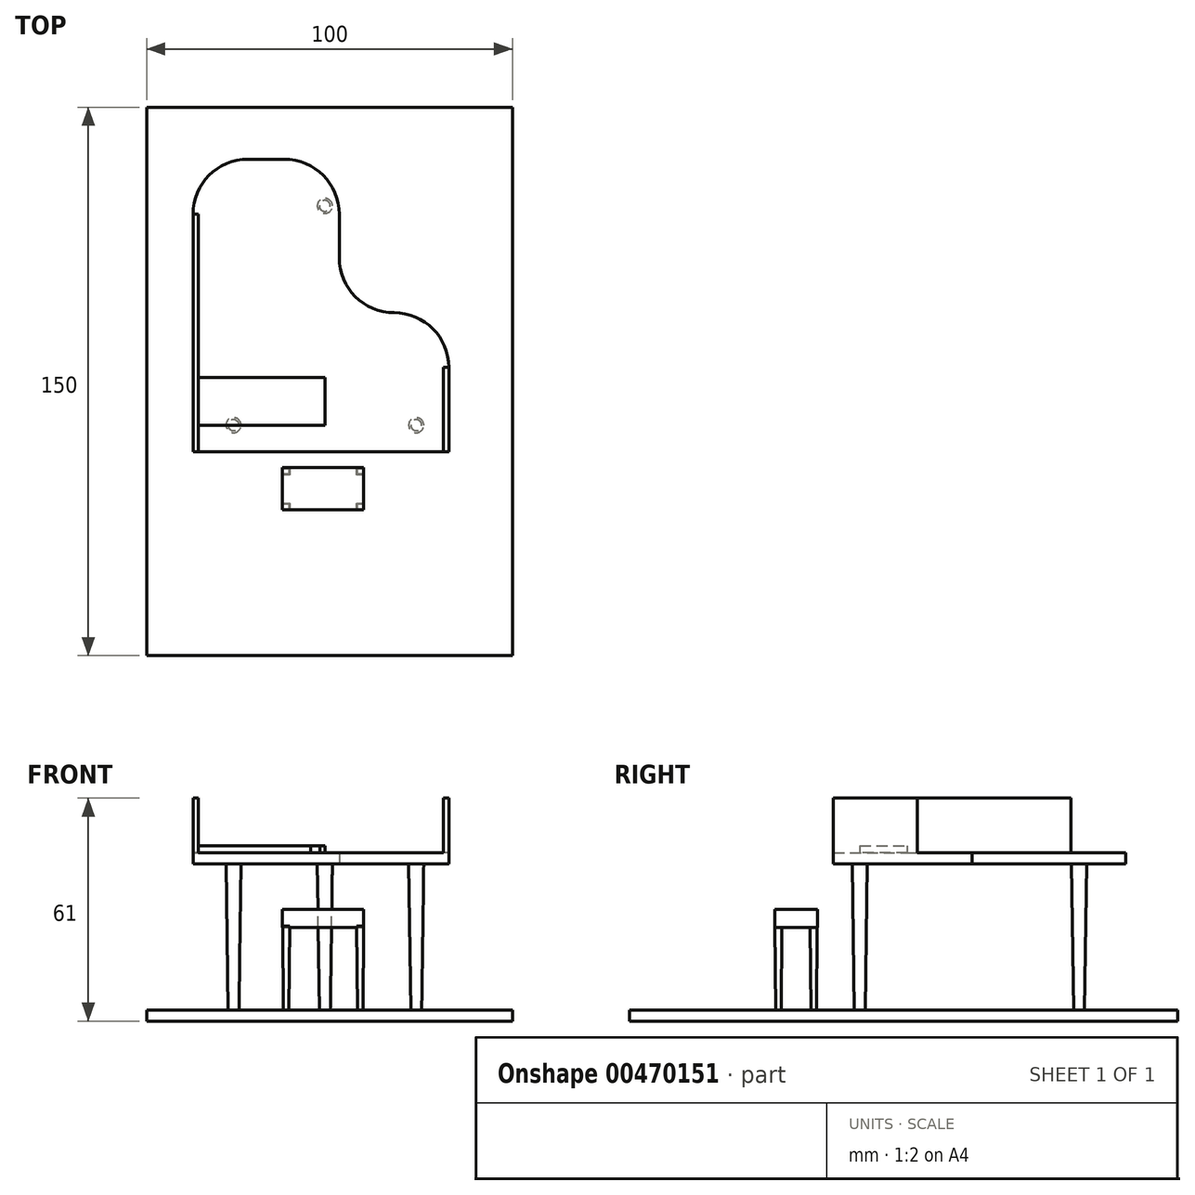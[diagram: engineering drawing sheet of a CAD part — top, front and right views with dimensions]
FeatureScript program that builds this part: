
annotation { "Feature Type Name" : "Feature", "Feature Type Description" : "" }
export const myFeature = defineFeature(function(context is Context, id is Id, definition is map)
    precondition{}
    {
        {
            var Q0;
            Q0=qCreatedBy(makeId("Top.planeOp"),FACE);
            var sketch = newSketch(context, id + "F0", { "sketchPlane" : qUnion([Q0])});
            skLineSegment(sketch, "E0.bottom", {"start": v(-48.7, 86.94) * mm, "end": v(51.3, 86.94) * mm});
            skLineSegment(sketch, "E0.top", {"start": v(-48.7, -63.06) * mm, "end": v(51.3, -63.06) * mm});
            skLineSegment(sketch, "E0.left", {"start": v(-48.7, 86.94) * mm, "end": v(-48.7, -63.06) * mm});
            skLineSegment(sketch, "E0.right", {"start": v(51.3, 86.94) * mm, "end": v(51.3, -63.06) * mm});
            skSolve(sketch);
        }
        {
            var Q0;
            Q0 = qSketchRegion(id + "F0", true);
            extrude(context, id + "F1", {"entities" : qUnion([Q0]), "depth" : 3 * mm});
        }
        {
            var Q0;
            Q0=makeQuery(id+"F1.opExtrude","CAP_FACE",FACE,{"disambiguationData":[OSD([sQuery(id+"F0.wireOp",EDGE,"E0.bottom"),sQuery(id+"F0.wireOp",EDGE,"E0.top"),sQuery(id+"F0.wireOp",EDGE,"E0.left"),sQuery(id+"F0.wireOp",EDGE,"E0.right")])],"isStart":false});
            var sketch = newSketch(context, id + "F2", { "sketchPlane" : qUnion([Q0])});
            skCircle(sketch, "E1", {"center": v(0, 60) * mm, "radius": 1.5 * mm});
            skCircle(sketch, "E2", {"center": v(-25, 0) * mm, "radius": 1.5 * mm});
            skCircle(sketch, "E3", {"center": v(25, 0) * mm, "radius": 1.5 * mm});
            skSolve(sketch);
        }
        {
            var Q0;
            Q0 = qSketchRegion(id + "F2", true);
            extrude(context, id + "F3", {"entities" : qUnion([Q0]), "operationType" : NewBodyOperationType.ADD, "depth" : 40 * mm, "hasDraft" : true, "draftAngle" : 0.8 * degree});
        }
        {
            var Q0;
            Q0=makeQuery(id+"F2.imprint","IMPRINT",FACE,{"disambiguationData":[TD([[makeQuery(id+"F2.imprint","IMPRINT",EDGE,{"derivedFrom":sQuery(id+"F2.wireOp",EDGE,"E1")}),-1.0]])]});
            var sketch = newSketch(context, id + "F4", { "sketchPlane" : qUnion([Q0])});
            skLineSegment(sketch, "E4.bottom", {"start": v(-11.36, -11.88) * mm, "end": v(-9.86, -11.88) * mm});
            skLineSegment(sketch, "E4.top", {"start": v(-11.36, -13.38) * mm, "end": v(-9.86, -13.38) * mm});
            skLineSegment(sketch, "E4.left", {"start": v(-11.36, -11.88) * mm, "end": v(-11.36, -13.38) * mm});
            skLineSegment(sketch, "E4.right", {"start": v(-9.86, -11.88) * mm, "end": v(-9.86, -13.38) * mm});
            skLineSegment(sketch, "E5.bottom", {"start": v(8.92, -11.88) * mm, "end": v(10.42, -11.88) * mm});
            skLineSegment(sketch, "E5.top", {"start": v(8.92, -13.38) * mm, "end": v(10.42, -13.38) * mm});
            skLineSegment(sketch, "E5.left", {"start": v(8.92, -11.88) * mm, "end": v(8.92, -13.38) * mm});
            skLineSegment(sketch, "E5.right", {"start": v(10.42, -11.88) * mm, "end": v(10.42, -13.38) * mm});
            skLineSegment(sketch, "E6.bottom", {"start": v(-11.36, -21.51) * mm, "end": v(-9.86, -21.51) * mm});
            skLineSegment(sketch, "E6.top", {"start": v(-11.36, -23.01) * mm, "end": v(-9.86, -23.01) * mm});
            skLineSegment(sketch, "E6.left", {"start": v(-11.36, -21.51) * mm, "end": v(-11.36, -23.01) * mm});
            skLineSegment(sketch, "E6.right", {"start": v(-9.86, -21.51) * mm, "end": v(-9.86, -23.01) * mm});
            skLineSegment(sketch, "E7.bottom", {"start": v(10.42, -21.51) * mm, "end": v(8.92, -21.51) * mm});
            skLineSegment(sketch, "E7.top", {"start": v(10.42, -23.01) * mm, "end": v(8.92, -23.01) * mm});
            skLineSegment(sketch, "E7.left", {"start": v(10.42, -21.51) * mm, "end": v(10.42, -23.01) * mm});
            skLineSegment(sketch, "E7.right", {"start": v(8.92, -21.51) * mm, "end": v(8.92, -23.01) * mm});
            skSolve(sketch);
        }
        {
            var Q0;
            Q0 = qSketchRegion(id + "F4", true);
            extrude(context, id + "F5", {"entities" : qUnion([Q0]), "operationType" : NewBodyOperationType.ADD, "depth" : 23 * mm, "hasDraft" : true, "draftAngle" : 0.5 * degree});
        }
        {
            var Q0;
            Q0=makeQuery(id+"F5.opExtrude","CAP_FACE",FACE,{"disambiguationData":[OSD([sQuery(id+"F4.wireOp",EDGE,"E4.bottom"),sQuery(id+"F4.wireOp",EDGE,"E4.top"),sQuery(id+"F4.wireOp",EDGE,"E4.left"),sQuery(id+"F4.wireOp",EDGE,"E4.right")])],"isStart":false});
            var sketch = newSketch(context, id + "F6", { "sketchPlane" : qUnion([Q0])});
            skLineSegment(sketch, "E8.bottom", {"start": v(-11.6, -11.63) * mm, "end": v(10.64, -11.63) * mm});
            skLineSegment(sketch, "E8.top", {"start": v(-11.6, -23.19) * mm, "end": v(10.64, -23.19) * mm});
            skLineSegment(sketch, "E8.left", {"start": v(-11.6, -11.63) * mm, "end": v(-11.6, -23.19) * mm});
            skLineSegment(sketch, "E8.right", {"start": v(10.64, -11.63) * mm, "end": v(10.64, -23.19) * mm});
            skSolve(sketch);
        }
        {
            var Q0;
            Q0 = qSketchRegion(id + "F6", true);
            extrude(context, id + "F7", {"entities" : qUnion([Q0]), "operationType" : NewBodyOperationType.ADD, "depth" : 4.6 * mm, "hasSecondDirection" : true, "secondDirectionOppositeDirection" : true, "secondDirectionDepth" : 0.4 * mm});
        }
        {
            var Q0;
            Q0=makeQuery(id+"F3.opExtrude","CAP_FACE",FACE,{"disambiguationData":[OSD([sQuery(id+"F2.wireOp",EDGE,"E1")])],"isStart":false});
            var sketch = newSketch(context, id + "F8", { "sketchPlane" : qUnion([Q0])});
            skLineSegment(sketch, "E9", {"start": v(-36.08, -7.22) * mm, "end": v(-36.08, 57.78) * mm});
            skLineSegment(sketch, "E10", {"start": v(-36.08, -7.22) * mm, "end": v(33.92, -7.22) * mm});
            skLineSegment(sketch, "E11", {"start": v(-21.08, 72.78) * mm, "end": v(-11.08, 72.78) * mm});
            skLineSegment(sketch, "E12", {"start": v(3.92, 57.78) * mm, "end": v(3.92, 45.78) * mm});
            skLineSegment(sketch, "E13", {"start": v(18.92, 30.78) * mm, "end": v(18.92, 30.78) * mm});
            skLineSegment(sketch, "E14", {"start": v(33.92, 15.78) * mm, "end": v(33.92, -7.22) * mm});
            skPoint(sketch, "E15.visualSharp", {"position": v(-36.08, 72.78) * mm});
            skArc(sketch, "E15.filletArc", {"start": v(-21.08, 72.78) * mm, "mid": v(-31.69, 68.38) * mm, "end": v(-36.08, 57.78) * mm});
            skPoint(sketch, "E16.visualSharp", {"position": v(3.92, 72.78) * mm});
            skArc(sketch, "E16.filletArc", {"start": v(3.92, 57.78) * mm, "mid": v(-0.47, 68.38) * mm, "end": v(-11.08, 72.78) * mm});
            skPoint(sketch, "E17.visualSharp", {"position": v(3.92, 30.78) * mm});
            skArc(sketch, "E17.filletArc", {"start": v(3.92, 45.78) * mm, "mid": v(8.31, 35.17) * mm, "end": v(18.92, 30.78) * mm});
            skPoint(sketch, "E18.visualSharp", {"position": v(33.92, 30.78) * mm});
            skArc(sketch, "E18.filletArc", {"start": v(33.92, 15.78) * mm, "mid": v(29.53, 26.38) * mm, "end": v(18.92, 30.78) * mm});
            skSolve(sketch);
        }
        {
            var Q0;
            Q0 = qSketchRegion(id + "F8", true);
            extrude(context, id + "F9", {"entities" : qUnion([Q0]), "operationType" : NewBodyOperationType.ADD, "depth" : 3 * mm});
        }
        {
            var Q0;
            Q0=makeQuery(id+"F9.opExtrude","CAP_FACE",FACE,{"disambiguationData":[OSD([sQuery(id+"F8.wireOp",EDGE,"E9"),sQuery(id+"F8.wireOp",EDGE,"E10"),sQuery(id+"F8.wireOp",EDGE,"E11"),sQuery(id+"F8.wireOp",EDGE,"E12"),sQuery(id+"F8.wireOp",EDGE,"E14"),sQuery(id+"F8.wireOp",EDGE,"E15.filletArc"),sQuery(id+"F8.wireOp",EDGE,"E16.filletArc"),sQuery(id+"F8.wireOp",EDGE,"E17.filletArc"),sQuery(id+"F8.wireOp",EDGE,"E18.filletArc")])],"isStart":false});
            var sketch = newSketch(context, id + "F10", { "sketchPlane" : qUnion([Q0])});
            skLineSegment(sketch, "E19.bottom", {"start": v(-36.08, -7.22) * mm, "end": v(-34.58, -7.22) * mm});
            skLineSegment(sketch, "E19.top", {"start": v(-36.08, 57.78) * mm, "end": v(-34.58, 57.78) * mm});
            skLineSegment(sketch, "E19.left", {"start": v(-36.08, -7.22) * mm, "end": v(-36.08, 57.78) * mm});
            skLineSegment(sketch, "E19.right", {"start": v(-34.58, -7.22) * mm, "end": v(-34.58, 57.78) * mm});
            skLineSegment(sketch, "E20.bottom", {"start": v(33.92, -7.22) * mm, "end": v(32.42, -7.22) * mm});
            skLineSegment(sketch, "E20.top", {"start": v(33.92, 15.78) * mm, "end": v(32.42, 15.78) * mm});
            skLineSegment(sketch, "E20.left", {"start": v(33.92, -7.22) * mm, "end": v(33.92, 15.78) * mm});
            skLineSegment(sketch, "E20.right", {"start": v(32.42, -7.22) * mm, "end": v(32.42, 15.78) * mm});
            skSolve(sketch);
        }
        {
            var Q0;
            Q0 = qSketchRegion(id + "F10", true);
            extrude(context, id + "F11", {"entities" : qUnion([Q0]), "operationType" : NewBodyOperationType.ADD, "depth" : 15 * mm});
        }
        {
            var Q0;
            Q0=makeQuery(id+"F9.opExtrude","CAP_FACE",FACE,{"disambiguationData":[OSD([sQuery(id+"F8.wireOp",EDGE,"E9"),sQuery(id+"F8.wireOp",EDGE,"E10"),sQuery(id+"F8.wireOp",EDGE,"E11"),sQuery(id+"F8.wireOp",EDGE,"E12"),sQuery(id+"F8.wireOp",EDGE,"E14"),sQuery(id+"F8.wireOp",EDGE,"E15.filletArc"),sQuery(id+"F8.wireOp",EDGE,"E16.filletArc"),sQuery(id+"F8.wireOp",EDGE,"E17.filletArc"),sQuery(id+"F8.wireOp",EDGE,"E18.filletArc")])],"isStart":false});
            var sketch = newSketch(context, id + "F12", { "sketchPlane" : qUnion([Q0])});
            skLineSegment(sketch, "E21.bottom", {"start": v(-34.58, 0) * mm, "end": v(-33.3, 0) * mm});
            skLineSegment(sketch, "E21.top", {"start": v(-34.58, 13) * mm, "end": v(-33.3, 13) * mm});
            skLineSegment(sketch, "E21.left", {"start": v(-34.58, 0) * mm, "end": v(-34.58, 13) * mm});
            skLineSegment(sketch, "E21.right", {"start": v(-33.3, 0) * mm, "end": v(-33.3, 13) * mm});
            skLineSegment(sketch, "E22.bottom", {"start": v(-33.3, 0) * mm, "end": v(-32.02, 0) * mm});
            skLineSegment(sketch, "E22.top", {"start": v(-33.3, 13) * mm, "end": v(-32.02, 13) * mm});
            skLineSegment(sketch, "E22.right", {"start": v(-32.02, 0) * mm, "end": v(-32.02, 13) * mm});
            skLineSegment(sketch, "E23.bottom", {"start": v(-32.02, 0) * mm, "end": v(-30.74, 0) * mm});
            skLineSegment(sketch, "E23.top", {"start": v(-32.02, 13) * mm, "end": v(-30.74, 13) * mm});
            skLineSegment(sketch, "E23.right", {"start": v(-30.74, 0) * mm, "end": v(-30.74, 13) * mm});
            skLineSegment(sketch, "E24.bottom", {"start": v(-30.74, 0) * mm, "end": v(-30.74, 0) * mm});
            skLineSegment(sketch, "E24.top", {"start": v(-30.74, 13) * mm, "end": v(-30.74, 13) * mm});
            skLineSegment(sketch, "E25.bottom", {"start": v(-30.74, 13) * mm, "end": v(-29.46, 13) * mm});
            skLineSegment(sketch, "E25.top", {"start": v(-30.74, 0) * mm, "end": v(-29.46, 0) * mm});
            skLineSegment(sketch, "E25.left", {"start": v(-30.74, 13) * mm, "end": v(-30.74, 0) * mm});
            skLineSegment(sketch, "E25.right", {"start": v(-29.46, 13) * mm, "end": v(-29.46, 0) * mm});
            skLineSegment(sketch, "E26.bottom", {"start": v(-29.46, 0) * mm, "end": v(-28.18, 0) * mm});
            skLineSegment(sketch, "E26.top", {"start": v(-29.46, 13) * mm, "end": v(-28.18, 13) * mm});
            skLineSegment(sketch, "E26.left", {"start": v(-29.46, 0) * mm, "end": v(-29.46, 13) * mm});
            skLineSegment(sketch, "E26.right", {"start": v(-28.18, 0) * mm, "end": v(-28.18, 13) * mm});
            skLineSegment(sketch, "E27.bottom", {"start": v(-28.18, 13) * mm, "end": v(-26.9, 13) * mm});
            skLineSegment(sketch, "E27.top", {"start": v(-28.18, 0) * mm, "end": v(-26.9, 0) * mm});
            skLineSegment(sketch, "E27.left", {"start": v(-28.18, 13) * mm, "end": v(-28.18, 0) * mm});
            skLineSegment(sketch, "E27.right", {"start": v(-26.9, 13) * mm, "end": v(-26.9, 0) * mm});
            skLineSegment(sketch, "E28.bottom", {"start": v(-26.9, 13) * mm, "end": v(-25.62, 13) * mm});
            skLineSegment(sketch, "E28.top", {"start": v(-26.9, 0) * mm, "end": v(-25.62, 0) * mm});
            skLineSegment(sketch, "E28.right", {"start": v(-25.62, 13) * mm, "end": v(-25.62, 0) * mm});
            skLineSegment(sketch, "E29.bottom", {"start": v(-25.62, 13) * mm, "end": v(-24.34, 13) * mm});
            skLineSegment(sketch, "E29.top", {"start": v(-25.62, 0) * mm, "end": v(-24.34, 0) * mm});
            skLineSegment(sketch, "E29.right", {"start": v(-24.34, 13) * mm, "end": v(-24.34, 0) * mm});
            skLineSegment(sketch, "E30.bottom", {"start": v(-24.34, 13) * mm, "end": v(-23.06, 13) * mm});
            skLineSegment(sketch, "E30.top", {"start": v(-24.34, 0) * mm, "end": v(-23.06, 0) * mm});
            skLineSegment(sketch, "E30.right", {"start": v(-23.06, 13) * mm, "end": v(-23.06, 0) * mm});
            skLineSegment(sketch, "E31.bottom", {"start": v(-23.06, 13) * mm, "end": v(-21.78, 13) * mm});
            skLineSegment(sketch, "E31.top", {"start": v(-23.06, 0) * mm, "end": v(-21.78, 0) * mm});
            skLineSegment(sketch, "E31.right", {"start": v(-21.78, 13) * mm, "end": v(-21.78, 0) * mm});
            skLineSegment(sketch, "E32.bottom", {"start": v(-21.78, 13) * mm, "end": v(-20.5, 13) * mm});
            skLineSegment(sketch, "E32.top", {"start": v(-21.78, 0) * mm, "end": v(-20.5, 0) * mm});
            skLineSegment(sketch, "E32.right", {"start": v(-20.5, 13) * mm, "end": v(-20.5, 0) * mm});
            skLineSegment(sketch, "E33.bottom", {"start": v(-20.5, 13) * mm, "end": v(-19.22, 13) * mm});
            skLineSegment(sketch, "E33.top", {"start": v(-20.5, 0) * mm, "end": v(-19.22, 0) * mm});
            skLineSegment(sketch, "E33.right", {"start": v(-19.22, 13) * mm, "end": v(-19.22, 0) * mm});
            skLineSegment(sketch, "E34.bottom", {"start": v(-19.22, 13) * mm, "end": v(-17.94, 13) * mm});
            skLineSegment(sketch, "E34.top", {"start": v(-19.22, 0) * mm, "end": v(-17.94, 0) * mm});
            skLineSegment(sketch, "E34.right", {"start": v(-17.94, 13) * mm, "end": v(-17.94, 0) * mm});
            skLineSegment(sketch, "E35.bottom", {"start": v(-17.94, 13) * mm, "end": v(-16.66, 13) * mm});
            skLineSegment(sketch, "E35.top", {"start": v(-17.94, 0) * mm, "end": v(-16.66, 0) * mm});
            skLineSegment(sketch, "E35.right", {"start": v(-16.66, 13) * mm, "end": v(-16.66, 0) * mm});
            skLineSegment(sketch, "E36.bottom", {"start": v(-16.66, 13) * mm, "end": v(-15.38, 13) * mm});
            skLineSegment(sketch, "E36.top", {"start": v(-16.66, 0) * mm, "end": v(-15.38, 0) * mm});
            skLineSegment(sketch, "E36.right", {"start": v(-15.38, 13) * mm, "end": v(-15.38, 0) * mm});
            skLineSegment(sketch, "E37.bottom", {"start": v(-15.38, 13) * mm, "end": v(-14.1, 13) * mm});
            skLineSegment(sketch, "E37.top", {"start": v(-15.38, 0) * mm, "end": v(-14.1, 0) * mm});
            skLineSegment(sketch, "E37.right", {"start": v(-14.1, 13) * mm, "end": v(-14.1, 0) * mm});
            skLineSegment(sketch, "E38.bottom", {"start": v(-14.1, 13) * mm, "end": v(-12.82, 13) * mm});
            skLineSegment(sketch, "E38.top", {"start": v(-14.1, 0) * mm, "end": v(-12.82, 0) * mm});
            skLineSegment(sketch, "E38.right", {"start": v(-12.82, 13) * mm, "end": v(-12.82, 0) * mm});
            skLineSegment(sketch, "E39.bottom", {"start": v(-12.82, 13) * mm, "end": v(-11.54, 13) * mm});
            skLineSegment(sketch, "E39.top", {"start": v(-12.82, 0) * mm, "end": v(-11.54, 0) * mm});
            skLineSegment(sketch, "E39.right", {"start": v(-11.54, 13) * mm, "end": v(-11.54, 0) * mm});
            skLineSegment(sketch, "E40.bottom", {"start": v(-11.54, 13) * mm, "end": v(-10.26, 13) * mm});
            skLineSegment(sketch, "E40.top", {"start": v(-11.54, 0) * mm, "end": v(-10.26, 0) * mm});
            skLineSegment(sketch, "E40.right", {"start": v(-10.26, 13) * mm, "end": v(-10.26, 0) * mm});
            skLineSegment(sketch, "E41.bottom", {"start": v(-10.26, 13) * mm, "end": v(-8.98, 13) * mm});
            skLineSegment(sketch, "E41.top", {"start": v(-10.26, 0) * mm, "end": v(-8.98, 0) * mm});
            skLineSegment(sketch, "E41.right", {"start": v(-8.98, 13) * mm, "end": v(-8.98, 0) * mm});
            skLineSegment(sketch, "E42.bottom", {"start": v(-8.98, 13) * mm, "end": v(-7.7, 13) * mm});
            skLineSegment(sketch, "E42.top", {"start": v(-8.98, 0) * mm, "end": v(-7.7, 0) * mm});
            skLineSegment(sketch, "E42.right", {"start": v(-7.7, 13) * mm, "end": v(-7.7, 0) * mm});
            skLineSegment(sketch, "E43.bottom", {"start": v(-7.7, 13) * mm, "end": v(-6.42, 13) * mm});
            skLineSegment(sketch, "E43.top", {"start": v(-7.7, 0) * mm, "end": v(-6.42, 0) * mm});
            skLineSegment(sketch, "E43.right", {"start": v(-6.42, 13) * mm, "end": v(-6.42, 0) * mm});
            skLineSegment(sketch, "E44.bottom", {"start": v(-6.42, 13) * mm, "end": v(-5.14, 13) * mm});
            skLineSegment(sketch, "E44.top", {"start": v(-6.42, 0) * mm, "end": v(-5.14, 0) * mm});
            skLineSegment(sketch, "E44.right", {"start": v(-5.14, 13) * mm, "end": v(-5.14, 0) * mm});
            skLineSegment(sketch, "E45.bottom", {"start": v(-5.14, 13) * mm, "end": v(-3.86, 13) * mm});
            skLineSegment(sketch, "E45.top", {"start": v(-5.14, 0) * mm, "end": v(-3.86, 0) * mm});
            skLineSegment(sketch, "E45.right", {"start": v(-3.86, 13) * mm, "end": v(-3.86, 0) * mm});
            skLineSegment(sketch, "E46.bottom", {"start": v(-3.86, 13) * mm, "end": v(-2.58, 13) * mm});
            skLineSegment(sketch, "E46.top", {"start": v(-3.86, -0.03) * mm, "end": v(-2.58, -0.03) * mm});
            skLineSegment(sketch, "E46.left", {"start": v(-3.86, 13) * mm, "end": v(-3.86, -0.03) * mm});
            skLineSegment(sketch, "E46.right", {"start": v(-2.58, 13) * mm, "end": v(-2.58, -0.03) * mm});
            skLineSegment(sketch, "E47.bottom", {"start": v(-2.58, 13) * mm, "end": v(-1.3, 13) * mm});
            skLineSegment(sketch, "E47.top", {"start": v(-2.58, -0.03) * mm, "end": v(-1.3, -0.03) * mm});
            skLineSegment(sketch, "E47.right", {"start": v(-1.3, 13) * mm, "end": v(-1.3, -0.03) * mm});
            skLineSegment(sketch, "E48.bottom", {"start": v(-1.3, 13) * mm, "end": v(-1.3, 13) * mm});
            skLineSegment(sketch, "E48.top", {"start": v(-1.3, 0) * mm, "end": v(-1.3, 0) * mm});
            skLineSegment(sketch, "E48.left", {"start": v(-1.3, 13) * mm, "end": v(-1.3, 0) * mm});
            skLineSegment(sketch, "E48.right", {"start": v(-1.3, 13) * mm, "end": v(-1.3, 0) * mm});
            skLineSegment(sketch, "E49.bottom", {"start": v(-1.3, 13) * mm, "end": v(0, 13) * mm});
            skLineSegment(sketch, "E49.top", {"start": v(-1.3, 0) * mm, "end": v(0, 0) * mm});
            skLineSegment(sketch, "E49.right", {"start": v(0, 13) * mm, "end": v(0, 0) * mm});
            skSolve(sketch);
        }
        {
            var Q0;
            Q0 = qSketchRegion(id + "F12", true);
            extrude(context, id + "F13", {"entities" : qUnion([Q0]), "operationType" : NewBodyOperationType.ADD, "depth" : 2 * mm});
        }
    });
